# Revit family: 1444xxx Miura Wall - CE
name_source: partatom
category: Lighting Fixtures
units: mm (PartAtom-declared; Revit-internal decimal feet)

## family parameters
Always vertical = Yes
Cut with Voids When Loaded = No
Host = Wall
Light Source = Yes
OmniClass Number = 23.80.70.00
OmniClass Title = Lighting
Part Type = Normal
Room Calculation Point = No
Round Connector Dimension = Use Diameter
Shared = No

## types (3) — shared parameters
Apparent Load = 0 VA
Color Filter = 16777215
Dimming Lamp Color Temperature Shift = <None>
Driver Required = No
Main Material = Metal - Steel
Manufacturer = Astro Lighting Ltd
Manufacturer URL - Europe and Rest of World = www.astrolighting.com
Manufacturer URL - North America = us.astrolighting.com
URL = www.astrolighting.com
zero-valued in all types: Default Elevation

## per-type parameters (varying)
| type | ADA compliant | Dimmable | Dimming Method | Driver Included | Efficacy (lm/w) | Electrical Class | Lamp | Length of Cable Supplied | Location / IP Rating | Main Finish | Photometric Web File | Power (Watts) | Product CCT | Product CRI | Product Dimensions (MM) | Product Location | Product Name | Product SKU | Product Weight (KG) | Tilt Angle |
| CE | N / A |  |  |  |  | 1 |  |  |  |  | generic |  | 2700K / 3000K | 80 / 90 |  |  |  | 1234001 |  | 60.00° |
| ETL |  |  |  |  |  | 0 |  |  | DAMP |  | generic |  | 2700K / 3000K | 80 / 90 |  | Bathroom |  | 1234001 |  | 60.00° |
| 1444xxx Miura Wall | Not Applicable | No | Not Applicable | Yes (Integral) | 49 | 1 | LED | Not Applicable | IP20 | Matt Black | 1444001_Miura Wall__Photometry_IES_Iss.01.ies | 7.5 | 2700K | 80 | 149x110x145 | Interior/Wall | Miura Wall | 1444001 | 0.58 | 90.00° |

## geometry (parser evidence)
native form markers: Sweep x3
no freeform markers — native parametric forms only
